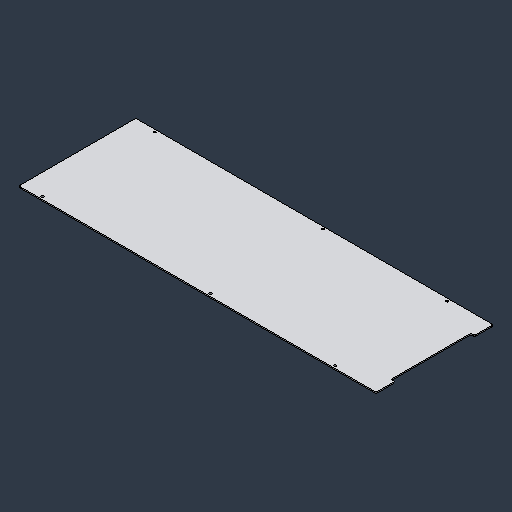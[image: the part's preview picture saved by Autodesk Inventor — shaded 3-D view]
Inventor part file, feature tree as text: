
AUTODESK INVENTOR PART (.ipt)
format: ipt  version: 2024.3 (Build 283343000, 343)  size: 90,624 bytes
history: native  units: mm (DEFAULTED — no unit token found)
features: fillet x1
ambient origin geometry x8: Origin, YZ Plane, XZ Plane, XY Plane, X Axis, Y Axis, Z Axis, Center Point
bodies: Solid1 (feature_tree)
feature tree (1):
  fillet  "Fillet2"  [1 undecoded]
note: 1 required parameter value undecoded (feature->parameter linkage not recoverable at this tier; creation-order binding heuristic only, values carry confidence <= 0.55)
